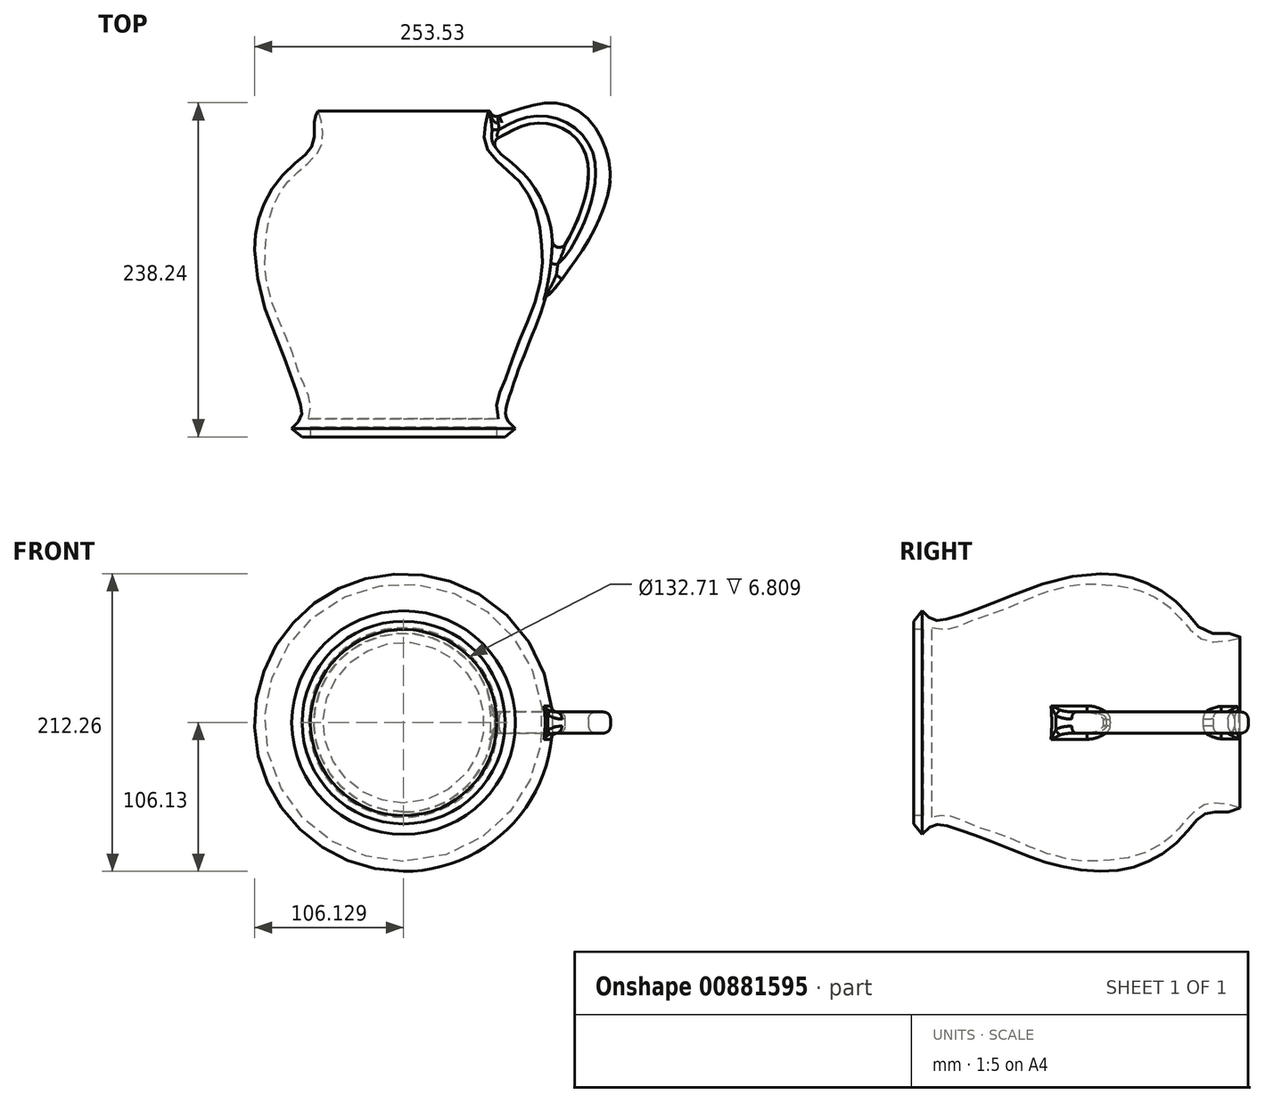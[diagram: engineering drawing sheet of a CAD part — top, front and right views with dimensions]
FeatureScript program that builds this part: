
annotation { "Feature Type Name" : "Feature", "Feature Type Description" : "" }
export const myFeature = defineFeature(function(context is Context, id is Id, definition is map)
    precondition{}
    {
        {
            var Q0;
            Q0=qCreatedBy(makeId("Top.planeOp"),FACE);
            var sketch = newSketch(context, id + "F0", { "sketchPlane" : qUnion([Q0])});
            skLineSegment(sketch, "E0", {"start": v(36.86, -36.27) * mm, "end": v(103.21, -36.27) * mm});
            skLineSegment(sketch, "E1", {"start": v(103.21, -36.27) * mm, "end": v(103.21, -43.08) * mm});
            skLineSegment(sketch, "E2", {"start": v(103.21, -43.08) * mm, "end": v(109.1, -43.08) * mm});
            skLineSegment(sketch, "E3", {"start": v(109.1, -43.08) * mm, "end": v(116.5, -37.15) * mm});
            skLineSegment(sketch, "E4", {"start": v(36.86, -36.27) * mm, "end": v(36.86, -30.03) * mm});
            skFitSpline(sketch, "E5", {"points": [v(116.5, -37.15) * mm, v(111.37, -31.67) * mm, v(109.51, -26.96) * mm, v(110.13, -21.12) * mm, v(114.23, -7.97) * mm, v(120.8, 10.28) * mm, v(132.49, 39.79) * mm, v(138.16, 57.04) * mm, v(142.65, 83.27) * mm, v(141.7, 105.96) * mm, v(136.24, 123.06) * mm, v(126.26, 140) * mm, v(110.83, 154.82) * mm, v(103.87, 161.18) * mm, v(100.54, 168.74) * mm, v(100.84, 176.9) * mm, v(97.82, 189.31) * mm, v(94.5, 173.88) * mm, v(94.8, 165.71) * mm, v(99.33, 157.85) * mm, v(107.8, 149.68) * mm, v(116.5, 141.82) * mm, v(123.53, 133.35) * mm, v(132.6, 112.47) * mm, v(135.33, 89.78) * mm, v(135.63, 76.47) * mm, v(129.14, 48.69) * mm, v(116.5, 18.46) * mm, v(111.68, 3.16) * mm, v(103.98, -15.32) * mm, v(103.21, -22.88) * mm, v(104.47, -30.03) * mm], "startDerivative": vector(-251.54, 236.58) * mm, "endDerivative": vector(207.16, -305.42) * mm});
            skLineSegment(sketch, "E6", {"start": v(36.86, -30.03) * mm, "end": v(104.47, -30.03) * mm});
            skSolve(sketch);
        }
        {
            var Q0;
            Q0=qCreatedBy(makeId("Top.planeOp"),FACE);
            var sketch = newSketch(context, id + "F1", { "sketchPlane" : qUnion([Q0])});
            skLineSegment(sketch, "E7", {"start": v(138.39, 81.43) * mm, "end": v(138.39, 69.02) * mm});
            skLineSegment(sketch, "E8", {"start": v(138.39, 69.02) * mm, "end": v(135.43, 60.74) * mm});
            skFitSpline(sketch, "E9", {"points": [v(135.43, 60.74) * mm, v(138.04, 57.36) * mm, v(154.7, 76.36) * mm, v(169.53, 98.75) * mm, v(179.98, 121.9) * mm, v(184.26, 142.94) * mm, v(179.9, 164.72) * mm, v(168.43, 183.7) * mm, v(152.05, 193.83) * mm, v(131.3, 193.96) * mm, v(97.8, 182.67) * mm], "startDerivative": vector(42.5, -115.4) * mm, "endDerivative": vector(-265.1, -112.2) * mm});
            skLineSegment(sketch, "E10", {"start": v(97.8, 182.67) * mm, "end": v(97.8, 167.09) * mm});
            skFitSpline(sketch, "E11", {"points": [v(97.8, 167.09) * mm, v(105.2, 170.6) * mm, v(120, 178) * mm, v(135.58, 180.72) * mm, v(154.27, 174.49) * mm, v(166.74, 158.13) * mm, v(167.9, 136.7) * mm, v(160.11, 110.22) * mm, v(145.31, 85.3) * mm, v(138.39, 81.43) * mm], "startDerivative": vector(89.56, 39.76) * mm, "endDerivative": vector(-89.5, -29.7) * mm});
            skSolve(sketch);
        }
        {
            var Q0;
            Q0=makeQuery(id+"F0.imprint","IMPRINT",FACE,{"disambiguationData":[TD([[makeQuery(id+"F0.imprint","IMPRINT",EDGE,{"derivedFrom":sQuery(id+"F0.wireOp",EDGE,"E0")}),1.0]])]});
            var Q1;
            Q1=sQuery(id+"F0.wireOp",EDGE,"E4");
            revolve(context, id + "F2", {"surfaceOperationType" : NewSurfaceOperationType.NEW, "entities" : qUnion([Q0]), "axis" : qUnion([Q1]), "revolveType" : RevolveType.FULL});
        }
        {
            var Q0;
            Q0=makeQuery(id+"F1.imprint","IMPRINT",FACE,{"disambiguationData":[TD([[makeQuery(id+"F1.imprint","IMPRINT",EDGE,{"derivedFrom":sQuery(id+"F1.wireOp",EDGE,"E7")}),1.0]])]});
            extrude(context, id + "F3", {"entities" : qUnion([Q0]), "operationType" : NewBodyOperationType.ADD, "endBound" : BoundingType.SYMMETRIC, "depth" : 15 * mm, "offsetDistance" : 25 * mm});
        }
        {
            var Q0;
            Q0=makeQuery(id+"F3.opExtrude","CAP_EDGE",EDGE,{"disambiguationData":[OSD([sQuery(id+"F1.wireOp",EDGE,"E11")])],"isStart":false});
            var Q1;
            Q1=makeQuery(id+"F3.opExtrude","CAP_EDGE",EDGE,{"disambiguationData":[OSD([sQuery(id+"F1.wireOp",EDGE,"E11")])],"isStart":true});
            fillet(context, id + "F4", {"entities" : qUnion([Q0, Q1]), "radius" : 5 * mm, "allowEdgeOverflow" : false});
        }
        {
            var Q0;
            Q0=makeQuery(id+"F3.boolean.opBoolean","INTERSECT",EDGE,{"disambiguationData":[OD(1.0)],"derivedFrom":[makeQuery(id+"F2.opRevolve","SWEPT_FACE",FACE,{"disambiguationData":[OSD([sQuery(id+"F0.wireOp",EDGE,"E5")])]}),makeQuery(id+"F3.opExtrude","SWEPT_FACE",FACE,{"disambiguationData":[OSD([sQuery(id+"F1.wireOp",EDGE,"E9")])]})]});
            var Q1;
            Q1=makeQuery(id+"F3.boolean.opBoolean","INTERSECT",EDGE,{"disambiguationData":[OD(1.0)],"derivedFrom":[makeQuery(id+"F2.opRevolve","SWEPT_FACE",FACE,{"disambiguationData":[OSD([sQuery(id+"F0.wireOp",EDGE,"E5")])]}),makeQuery(id+"F3.opExtrude","CAP_FACE",FACE,{"disambiguationData":[OSD([sQuery(id+"F1.wireOp",EDGE,"E7"),sQuery(id+"F1.wireOp",EDGE,"E8"),sQuery(id+"F1.wireOp",EDGE,"E9"),sQuery(id+"F1.wireOp",EDGE,"E10"),sQuery(id+"F1.wireOp",EDGE,"E11")])],"isStart":false})]});
            var Q2;
            Q2=makeQuery(id+"F3.boolean.opBoolean","INTERSECT",EDGE,{"disambiguationData":[OD(0.0)],"derivedFrom":[makeQuery(id+"F2.opRevolve","SWEPT_FACE",FACE,{"disambiguationData":[OSD([sQuery(id+"F0.wireOp",EDGE,"E5")])]}),makeQuery(id+"F3.opExtrude","CAP_FACE",FACE,{"disambiguationData":[OSD([sQuery(id+"F1.wireOp",EDGE,"E7"),sQuery(id+"F1.wireOp",EDGE,"E8"),sQuery(id+"F1.wireOp",EDGE,"E9"),sQuery(id+"F1.wireOp",EDGE,"E10"),sQuery(id+"F1.wireOp",EDGE,"E11")])],"isStart":false})]});
            var Q3;
            Q3=makeQuery(id+"F3.boolean.opBoolean","INTERSECT",EDGE,{"disambiguationData":[OD(0.0)],"derivedFrom":[makeQuery(id+"F2.opRevolve","SWEPT_FACE",FACE,{"disambiguationData":[OSD([sQuery(id+"F0.wireOp",EDGE,"E5")])]}),makeQuery(id+"F3.opExtrude","SWEPT_FACE",FACE,{"disambiguationData":[OSD([sQuery(id+"F1.wireOp",EDGE,"E9")])]})]});
            fillet(context, id + "F5", {"entities" : qUnion([Q0, Q1, Q2, Q3]), "radius" : 5 * mm, "tangentPropagation" : true, "allowEdgeOverflow" : false});
        }
        {
            var Q0;
            Q0=makeQuery(id+"F3.opExtrude","CAP_EDGE",EDGE,{"disambiguationData":[OSD([sQuery(id+"F1.wireOp",EDGE,"E9")])],"isStart":false});
            var Q1;
            Q1=makeQuery(id+"F3.opExtrude","CAP_EDGE",EDGE,{"disambiguationData":[OSD([sQuery(id+"F1.wireOp",EDGE,"E9")])],"isStart":true});
            fillet(context, id + "F6", {"entities" : qUnion([Q0, Q1]), "radius" : 5 * mm, "tangentPropagation" : true, "allowEdgeOverflow" : false});
        }
    });
